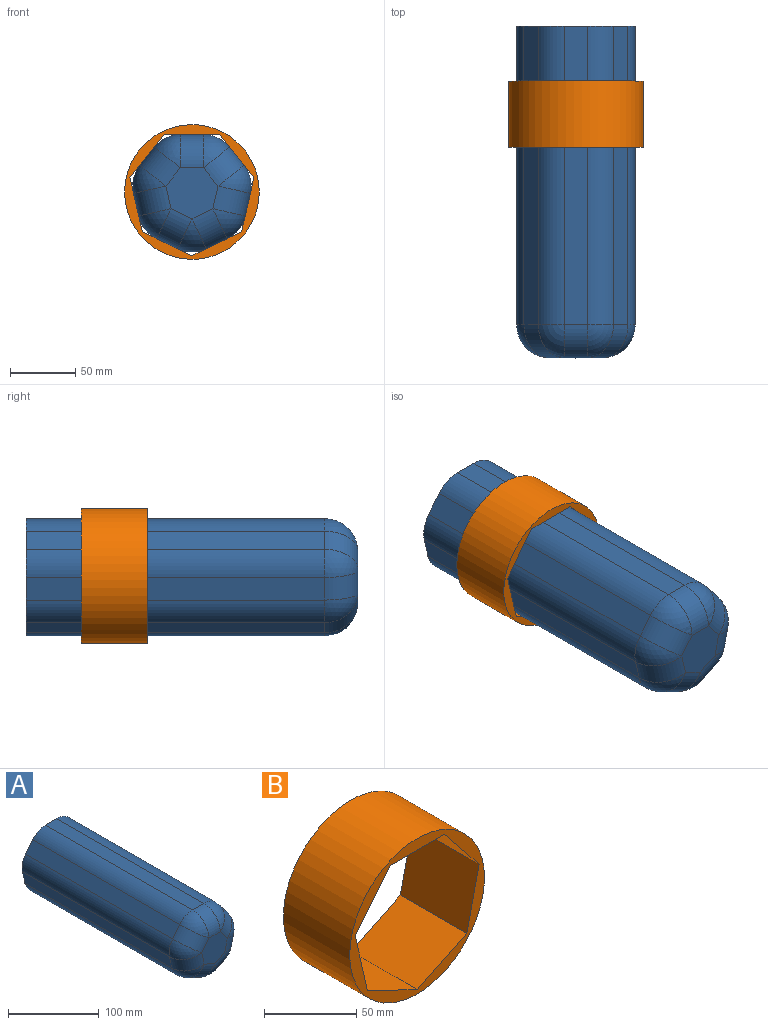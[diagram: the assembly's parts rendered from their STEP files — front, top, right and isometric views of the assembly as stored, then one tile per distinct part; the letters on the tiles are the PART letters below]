
ASSEMBLY  parts=2 mates=1
PART A: 30 faces, bbox 90.6x254x89.6 mm
  f0: plane 228.6x15.98mm, normal (-0.43,0,-0.9), area 4053.6mm2, adj f7,f23,f27,f29
  f1: plane 228.6x17.29mm, normal (-0.97,0,-0.22), area 4053.6mm2, adj f7,f20,f26,f29
  f2: plane 228.6x13.86mm, normal (-0.78,0,0.62), area 4053.6mm2, adj f7,f14,f20,f21
  f3: plane 228.6x17.73mm, normal (0,0,1), area 4053.6mm2, adj f7,f9,f14,f15
  f4: plane 228.6x13.86mm, normal (0.78,0,0.62), area 4053.6mm2, adj f7,f9,f10,f11
  f5: plane 228.6x17.29mm, normal (0.97,0,-0.22), area 4053.6mm2, adj f7,f11,f16,f17
  f6: plane 228.6x15.98mm, normal (0.43,0,-0.9), area 4053.6mm2, adj f7,f17,f22,f23
  f7: plane 90.64x89.64mm, normal (0,1,0), area 6322.2mm2, adj f0,f1,f2,f3,f4,f5,f6,f9
  f8: plane 39.84x38.84mm, normal (0,-1,0), area 1142.6mm2, adj f10,f15,f16,f21,f22,f26,f27
  f9: cylinder r=25.4mm len=228.6mm, axis (0,-1,0), area 5211.8mm2, adj f3,f4,f7,f12
  f10: cylinder r=25.4mm len=30.91mm, axis (0.62,0,-0.78), area 707.5mm2, adj f4,f8,f12,f13
  f11: cylinder r=25.4mm len=228.6mm, axis (0,-1,0), area 5211.8mm2, adj f4,f5,f7,f13
  f12: sphere r=25.4mm, area 579.1mm2, adj f9,f10,f15
  f13: sphere r=25.4mm, area 579.1mm2, adj f10,f11,f16
  f14: cylinder r=25.4mm len=228.6mm, axis (0,-1,0), area 5211.8mm2, adj f2,f3,f7,f18
  f15: cylinder r=25.4mm len=25.4mm, axis (1,0,0), area 707.5mm2, adj f3,f8,f12,f18
  f16: cylinder r=25.4mm len=28.71mm, axis (-0.22,0,-0.97), area 707.5mm2, adj f5,f8,f13,f19
  f17: cylinder r=25.4mm len=228.6mm, axis (0,-1,0), area 5211.8mm2, adj f5,f6,f7,f19
  f18: sphere r=25.4mm, area 579.1mm2, adj f14,f15,f21
  f19: sphere r=25.4mm, area 579.1mm2, adj f16,f17,f22
  f20: cylinder r=25.4mm len=228.6mm, axis (0,-1,0), area 5211.8mm2, adj f1,f2,f7,f24
  f21: cylinder r=25.4mm len=30.91mm, axis (0.62,0,0.78), area 707.5mm2, adj f2,f8,f18,f24
  f22: cylinder r=25.4mm len=30.58mm, axis (-0.9,0,-0.43), area 707.5mm2, adj f6,f8,f19,f25
  f23: cylinder r=25.4mm len=228.6mm, axis (0,-1,0), area 5211.8mm2, adj f0,f6,f7,f25
  f24: sphere r=25.4mm, area 579.1mm2, adj f20,f21,f26
  f25: sphere r=25.4mm, area 579.1mm2, adj f22,f23,f27
  f26: cylinder r=25.4mm len=28.71mm, axis (-0.22,0,0.97), area 707.5mm2, adj f1,f8,f24,f28
  f27: cylinder r=25.4mm len=30.58mm, axis (-0.9,0,0.43), area 707.5mm2, adj f0,f8,f25,f28
  f28: sphere r=25.4mm, area 579.1mm2, adj f26,f27,f29
  f29: cylinder r=25.4mm len=228.6mm, axis (0,-1,0), area 5211.8mm2, adj f0,f1,f7,f28
PART B: 10 faces, bbox 103.1x50.8x103.1 mm
  f0: plane 50.8x41.14mm, normal (0.97,0,0.22), area 2143.6mm2, adj f1,f6,f8,f9
  f1: plane 50.8x32.99mm, normal (0.78,0,-0.62), area 2143.6mm2, adj f0,f2,f8,f9
  f2: plane 50.8x42.2mm, normal (0,0,-1), area 2143.6mm2, adj f1,f3,f8,f9
  f3: plane 50.8x32.99mm, normal (-0.78,0,-0.62), area 2143.6mm2, adj f2,f4,f8,f9
  f4: plane 50.8x41.14mm, normal (-0.97,0,0.22), area 2143.6mm2, adj f3,f5,f8,f9
  f5: plane 50.8x38.02mm, normal (-0.43,0,0.9), area 2143.6mm2, adj f4,f6,f8,f9
  f6: plane 50.8x38.02mm, normal (0.43,0,0.9), area 2143.6mm2, adj f0,f5,f8,f9
  f7: cylinder r=51.52mm len=103.05mm, axis (0,1,0), area 16446mm2, adj f8,f9
  f8: plane 103.05x103.05mm, normal (0,-1,0), area 1870.1mm2, adj f0,f1,f2,f3,f4,f5,f6,f7
  f9: plane 103.05x103.05mm, normal (0,1,0), area 1870.1mm2, adj f0,f1,f2,f3,f4,f5,f6,f7
PLACE A t=(80.25,-58.37,48.68)mm
PLACE B t=(80.25,26.56,48.68)mm
MATE slider A.f8 <-> B.f7  axis (0,-1,0) through (80.25,-159.97,48.68)mm
